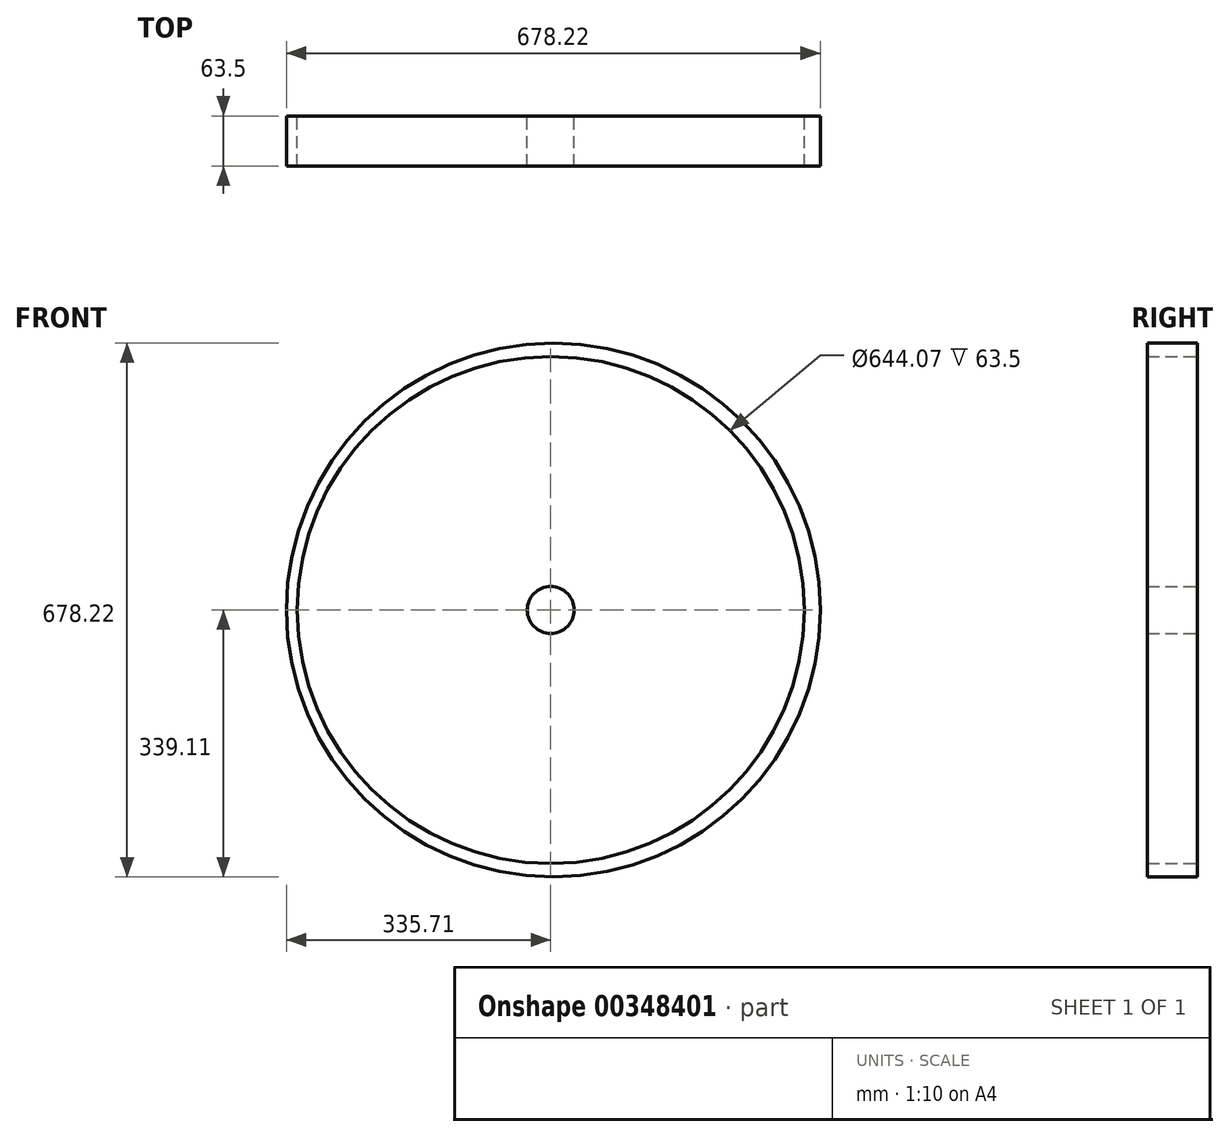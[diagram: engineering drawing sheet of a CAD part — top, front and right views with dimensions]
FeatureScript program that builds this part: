
annotation { "Feature Type Name" : "Feature", "Feature Type Description" : "" }
export const myFeature = defineFeature(function(context is Context, id is Id, definition is map)
    precondition{}
    {
        {
            var Q0;
            Q0=qCreatedBy(makeId("Front.planeOp"),FACE);
            var sketch = newSketch(context, id + "F0", { "sketchPlane" : qUnion([Q0])});
            skCircle(sketch, "E0", {"center": v(3.4, 0) * mm, "radius": 339.1 * mm});
            skCircle(sketch, "E1", {"center": v(0, 0) * mm, "radius": 29.81 * mm});
            skCircle(sketch, "E2", {"center": v(0, 0) * mm, "radius": 322.04 * mm});
            skSolve(sketch);
        }
        {
            var Q0;
            Q0=makeQuery(id+"F0.imprint","IMPRINT",FACE,{"disambiguationData":[TD([[makeQuery(id+"F0.imprint","IMPRINT",EDGE,{"derivedFrom":sQuery(id+"F0.wireOp",EDGE,"E0")}),1.0]])]});
            var Q1;
            Q1=makeQuery(id+"F0.imprint","IMPRINT",FACE,{"disambiguationData":[TD([[makeQuery(id+"F0.imprint","IMPRINT",EDGE,{"derivedFrom":sQuery(id+"F0.wireOp",EDGE,"E1")}),1.0]])]});
            extrude(context, id + "F1", {"entities" : qUnion([Q0, Q1]), "endBound" : BoundingType.SYMMETRIC, "depth" : 63.5 * mm});
        }
    });
